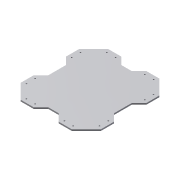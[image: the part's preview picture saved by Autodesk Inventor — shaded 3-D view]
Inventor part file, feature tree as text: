
AUTODESK INVENTOR PART (.ipt)
format: ipt  version: 2014 (Build 180170000, 170)  size: 145,920 bytes
history: native  units: mm
features: extrude x2, sketch x2, mirror x1
ambient origin geometry x8: Origin, YZ Plane, XZ Plane, XY Plane, X Axis, Y Axis, Z Axis, Center Point
bodies: Solid1 (feature_tree)
feature tree (5):
  extrude  "Extrusion1"  Depth=225.0mm
  extrude  "Extrusion2"  Depth=25.0mm
  mirror  "Mirror1"
  sketch  "Sketch1"  dims[d0=250.0mm d1=225.0mm]
  sketch  "Sketch2"  dims[d2=5.0mm d3=0.0mm d4=25.0mm d5=25.0mm d6=45.0mm d7=12.5mm d8=12.5mm d9=4.5mm d10=30.0mm d11=30.0mm d12=30.0mm d13=7.5mm d14=7.5mm d15=7.5mm d16=12.5mm d17=5.0mm d18=0.0mm]
